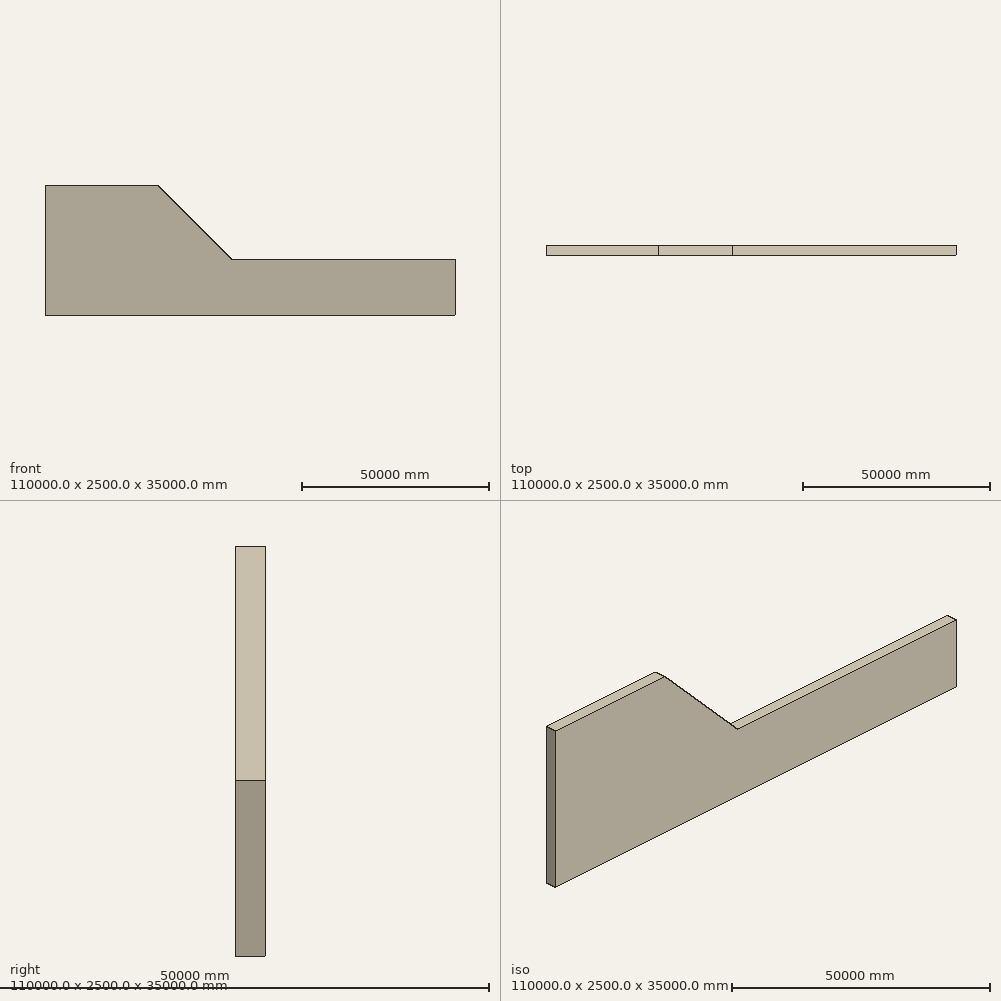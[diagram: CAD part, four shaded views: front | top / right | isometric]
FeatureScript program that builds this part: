
annotation { "Feature Type Name" : "Feature", "Feature Type Description" : "" }
export const myFeature = defineFeature(function(context is Context, id is Id, definition is map)
    precondition{}
    {
        {
            var Q0;
            Q0=qCreatedBy(makeId("Front.planeOp"),FACE);
            var sketch = newSketch(context, id + "F0", { "sketchPlane" : qUnion([Q0])});
            skLineSegment(sketch, "E0", {"start": v(0, 0) * mm, "end": v(110000, 0) * mm});
            skLineSegment(sketch, "E1", {"start": v(0, 0) * mm, "end": v(0, 35000) * mm});
            skLineSegment(sketch, "E2", {"start": v(0, 35000) * mm, "end": v(30000, 35000) * mm});
            skLineSegment(sketch, "E3", {"start": v(110000, 0) * mm, "end": v(110000, 15000) * mm});
            skLineSegment(sketch, "E4", {"start": v(30000, 35000) * mm, "end": v(50000, 15000) * mm});
            skLineSegment(sketch, "E5", {"start": v(50000, 15000) * mm, "end": v(110000, 15000) * mm});
            skSolve(sketch);
        }
        {
            var Q0;
            Q0=makeQuery(id+"F0.imprint","IMPRINT",FACE,{"disambiguationData":[TD([[makeQuery(id+"F0.imprint","IMPRINT",EDGE,{"derivedFrom":sQuery(id+"F0.wireOp",EDGE,"E0")}),1.0]])]});
            extrude(context, id + "F1", {"entities" : qUnion([Q0]), "depth" : 2500 * mm});
        }
    });
